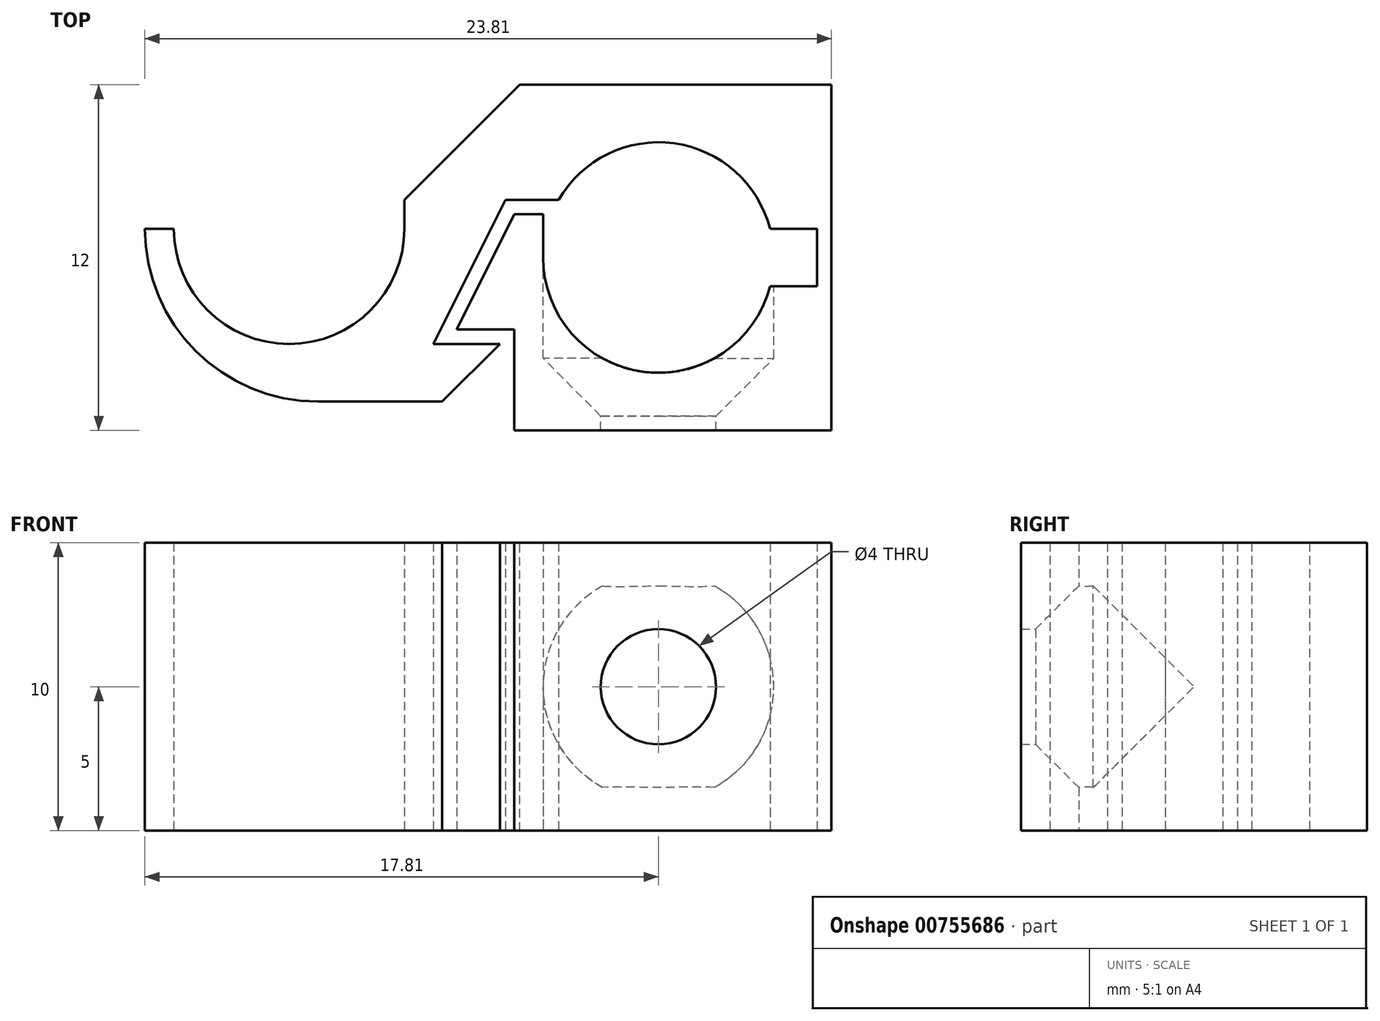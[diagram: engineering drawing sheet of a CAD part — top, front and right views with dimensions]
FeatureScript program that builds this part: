
annotation { "Feature Type Name" : "Feature", "Feature Type Description" : "" }
export const myFeature = defineFeature(function(context is Context, id is Id, definition is map)
    precondition{}
    {
        {
            var Q0;
            Q0=qCreatedBy(makeId("Top.planeOp"),FACE);
            var sketch = newSketch(context, id + "F0", { "sketchPlane" : qUnion([Q0])});
            skArc(sketch, "E0", {"start": v(-4, 0) * mm, "mid": v(3.86, -1.04) * mm, "end": v(-3.46, 2) * mm});
            skLineSegment(sketch, "E1", {"start": v(-5, 1.5) * mm, "end": v(-7, -2.5) * mm});
            skLineSegment(sketch, "E2", {"start": v(-7, -2.5) * mm, "end": v(-5, -2.5) * mm});
            skLineSegment(sketch, "E3", {"start": v(-5, -2.5) * mm, "end": v(-5, -6) * mm});
            skLineSegment(sketch, "E4", {"start": v(-5, -6) * mm, "end": v(6, -6) * mm});
            skLineSegment(sketch, "E5", {"start": v(6, -6) * mm, "end": v(6, 6) * mm});
            skCircle(sketch, "E6.0", {"center": v(0, 0) * mm, "radius": 6 * mm, "construction": true});
            skLineSegment(sketch, "E7", {"start": v(6, 6) * mm, "end": v(-8.8, 6) * mm});
            skLineSegment(sketch, "E8", {"start": v(-5, 1.5) * mm, "end": v(-4, 1.5) * mm});
            skLineSegment(sketch, "E9", {"start": v(-8.8, 6) * mm, "end": v(-8.8, 1) * mm});
            skLineSegment(sketch, "E10", {"start": v(-4, 1.5) * mm, "end": v(-4, 0) * mm});
            skLineSegment(sketch, "E11.0", {"start": v(-5.3, 2) * mm, "end": v(-3.46, 2) * mm});
            skLineSegment(sketch, "E11.1", {"start": v(-5.3, 2) * mm, "end": v(-7.8, -3) * mm});
            skLineSegment(sketch, "E12.0", {"start": v(-7.8, -3) * mm, "end": v(-5.5, -3) * mm});
            skLineSegment(sketch, "E13", {"start": v(-5.5, -3) * mm, "end": v(-5.5, -5) * mm});
            skLineSegment(sketch, "E14", {"start": v(-5.5, -5) * mm, "end": v(-8.8, -5) * mm});
            skLineSegment(sketch, "E15", {"start": v(-8.8, -5) * mm, "end": v(-17.8, -5) * mm});
            skLineSegment(sketch, "E16", {"start": v(-17.8, -5) * mm, "end": v(-17.8, 1) * mm});
            skLineSegment(sketch, "E17", {"start": v(-17.8, 1) * mm, "end": v(-16.8, 1) * mm});
            skArc(sketch, "E18", {"start": v(-16.8, 1) * mm, "mid": v(-12.8, -3) * mm, "end": v(-8.8, 1) * mm});
            skPoint(sketch, "E19", {"position": v(-12.8, -3) * mm});
            skPoint(sketch, "E20", {"position": v(4, 0) * mm});
            skLineSegment(sketch, "E21.bottom", {"start": v(2.5, 1) * mm, "end": v(5.5, 1) * mm});
            skLineSegment(sketch, "E21.top", {"start": v(2.5, -1) * mm, "end": v(5.5, -1) * mm});
            skLineSegment(sketch, "E21.left", {"start": v(2.5, 1) * mm, "end": v(2.5, -1) * mm});
            skLineSegment(sketch, "E21.right", {"start": v(5.5, 1) * mm, "end": v(5.5, -1) * mm});
            skSolve(sketch);
        }
        {
            var Q0;
            Q0=makeQuery(id+"F0.imprint","IMPRINT",FACE,{"disambiguationData":[TD([[makeQuery(id+"F0.imprint","IMPRINT",EDGE,{"derivedFrom":sQuery(id+"F0.wireOp",EDGE,"E1")}),1.0]])]});
            extrude(context, id + "F1", {"entities" : qUnion([Q0]), "endBound" : BoundingType.SYMMETRIC, "depth" : 10 * mm, "offsetDistance" : 25 * mm});
        }
        {
            var Q0;
            Q0=qCreatedBy(makeId("Top.planeOp"),FACE);
            var sketch = newSketch(context, id + "F2", { "sketchPlane" : qUnion([Q0])});
            skLineSegment(sketch, "E22", {"start": v(0, 0) * mm, "end": v(0, -6) * mm, "construction": true});
            skPoint(sketch, "E23", {"position": v(-4, 1.5) * mm});
            skLineSegment(sketch, "E24", {"start": v(-4, 1.5) * mm, "end": v(-4, -3.5) * mm});
            skLineSegment(sketch, "E25", {"start": v(-4, -3.5) * mm, "end": v(-2, -5.5) * mm});
            skLineSegment(sketch, "E26", {"start": v(-2, -5.5) * mm, "end": v(-2, -6) * mm});
            skLineSegment(sketch, "E27", {"start": v(-2, -6) * mm, "end": v(0, -6) * mm});
            skLineSegment(sketch, "E28", {"start": v(-4, 1.5) * mm, "end": v(0, 1.5) * mm});
            skLineSegment(sketch, "E29", {"start": v(0, 1.5) * mm, "end": v(0, -6) * mm});
            skLineSegment(sketch, "E30", {"start": v(0.13, 0) * mm, "end": v(-4, 0) * mm});
            skSolve(sketch);
        }
        {
            var Q0;
            {var subQ1=sQuery(id+"F2.wireOp",EDGE,"E25");Q0=makeQuery(id+"F2.imprint","IMPRINT",FACE,{"disambiguationData":[TD([[makeQuery(id+"F2.imprint","IMPRINT",EDGE,{"derivedFrom":subQ1}),1.0]])]});}
            var Q1;
            Q1=sQuery(id+"F2.wireOp",EDGE,"E29");
            revolve(context, id + "F3", {"operationType" : NewBodyOperationType.REMOVE, "surfaceOperationType" : NewSurfaceOperationType.NEW, "entities" : qUnion([Q0]), "axis" : qUnion([Q1]), "revolveType" : RevolveType.FULL});
        }
        {
            var Q0;
            Q0=makeQuery(id+"F1.opExtrude","SWEPT_EDGE",EDGE,{"disambiguationData":[OSD([sQuery(id+"F0.wireOp",EDGE,"E13"),sQuery(id+"F0.wireOp",EDGE,"E14")])]});
            chamfer(context, id + "F4", {"entities" : qUnion([Q0]), "width" : 2 * mm, "tangentPropagation" : true});
        }
        {
            var Q0;
            Q0=makeQuery(id+"F1.opExtrude","SWEPT_EDGE",EDGE,{"disambiguationData":[OSD([sQuery(id+"F0.wireOp",EDGE,"E15"),sQuery(id+"F0.wireOp",EDGE,"E16")])]});
            fillet(context, id + "F5", {"entities" : qUnion([Q0]), "radius" : 6 * mm, "tangentPropagation" : true, "allowEdgeOverflow" : false});
        }
        {
            var Q0;
            Q0=makeQuery(id+"F1.opExtrude","SWEPT_EDGE",EDGE,{"disambiguationData":[OSD([sQuery(id+"F0.wireOp",EDGE,"E7"),sQuery(id+"F0.wireOp",EDGE,"E9")])]});
            chamfer(context, id + "F6", {"entities" : qUnion([Q0]), "width" : 4 * mm, "tangentPropagation" : true});
        }
    });
